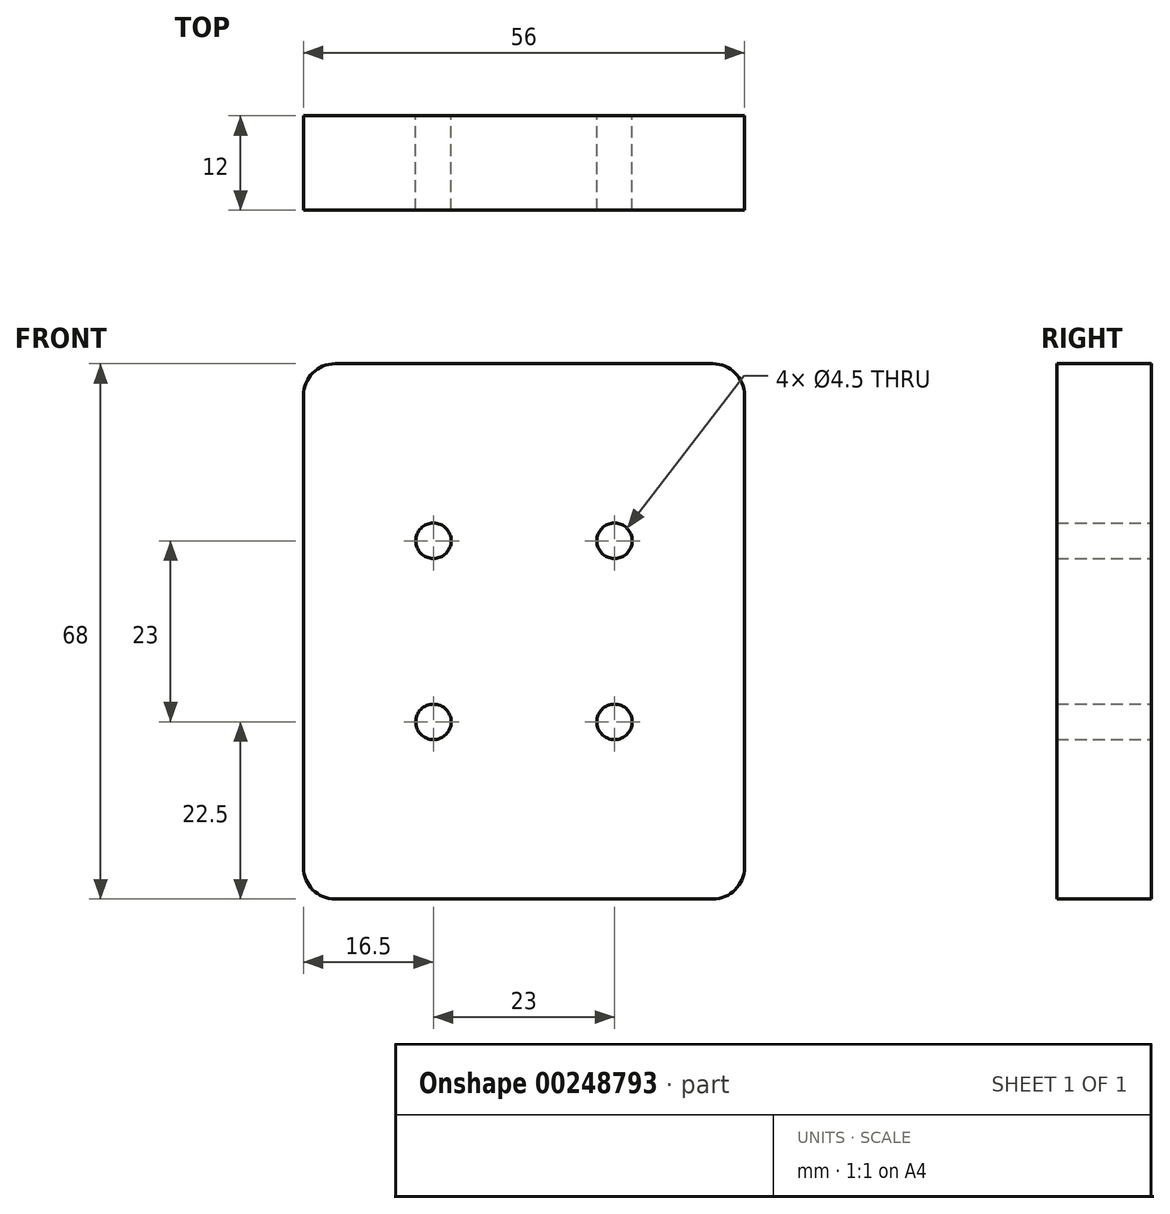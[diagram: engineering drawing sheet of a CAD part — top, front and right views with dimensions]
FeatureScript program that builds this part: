
annotation { "Feature Type Name" : "Feature", "Feature Type Description" : "" }
export const myFeature = defineFeature(function(context is Context, id is Id, definition is map)
    precondition{}
    {
        {
            var Q0;
            Q0=qCreatedBy(makeId("Front.planeOp"),FACE);
            var sketch = newSketch(context, id + "F0", { "sketchPlane" : qUnion([Q0])});
            skLineSegment(sketch, "E0.bottom", {"start": v(28, 34) * mm, "end": v(-28, 34) * mm});
            skLineSegment(sketch, "E0.top", {"start": v(28, -34) * mm, "end": v(-28, -34) * mm});
            skLineSegment(sketch, "E0.left", {"start": v(28, 34) * mm, "end": v(28, -34) * mm});
            skLineSegment(sketch, "E0.right", {"start": v(-28, 34) * mm, "end": v(-28, -34) * mm});
            skPoint(sketch, "E0.middle", {"position": v(0, 0) * mm});
            skCircle(sketch, "E1", {"center": v(-11.5, 11.5) * mm, "radius": 2.25 * mm});
            skCircle(sketch, "E2.MirrorC", {"center": v(11.5, 11.5) * mm, "radius": 2.25 * mm});
            skCircle(sketch, "E3.MirrorC", {"center": v(11.5, -11.5) * mm, "radius": 2.25 * mm});
            skCircle(sketch, "E4.MirrorC", {"center": v(-11.5, -11.5) * mm, "radius": 2.25 * mm});
            skSolve(sketch);
        }
        {
            var Q0;
            Q0=makeQuery(id+"F0.imprint","IMPRINT",FACE,{"disambiguationData":[TD([[makeQuery(id+"F0.imprint","IMPRINT",EDGE,{"derivedFrom":sQuery(id+"F0.wireOp",EDGE,"E0.bottom")}),1.0]])]});
            extrude(context, id + "F1", {"entities" : qUnion([Q0]), "depth" : 12 * mm, "offsetDistance" : 25 * mm});
        }
        {
            var Q0;
            Q0=makeQuery(id+"F1.opExtrude","SWEPT_EDGE",EDGE,{"disambiguationData":[OSD([sQuery(id+"F0.wireOp",EDGE,"E0.top"),sQuery(id+"F0.wireOp",EDGE,"E0.left")])]});
            var Q1;
            Q1=makeQuery(id+"F1.opExtrude","SWEPT_EDGE",EDGE,{"disambiguationData":[OSD([sQuery(id+"F0.wireOp",EDGE,"E0.top"),sQuery(id+"F0.wireOp",EDGE,"E0.right")])]});
            var Q2;
            Q2=makeQuery(id+"F1.opExtrude","SWEPT_EDGE",EDGE,{"disambiguationData":[OSD([sQuery(id+"F0.wireOp",EDGE,"E0.bottom"),sQuery(id+"F0.wireOp",EDGE,"E0.left")])]});
            var Q3;
            Q3=makeQuery(id+"F1.opExtrude","SWEPT_EDGE",EDGE,{"disambiguationData":[OSD([sQuery(id+"F0.wireOp",EDGE,"E0.bottom"),sQuery(id+"F0.wireOp",EDGE,"E0.right")])]});
            fillet(context, id + "F2", {"entities" : qUnion([Q0, Q1, Q2, Q3]), "radius" : 4 * mm, "tangentPropagation" : true, "allowEdgeOverflow" : false});
        }
    });
